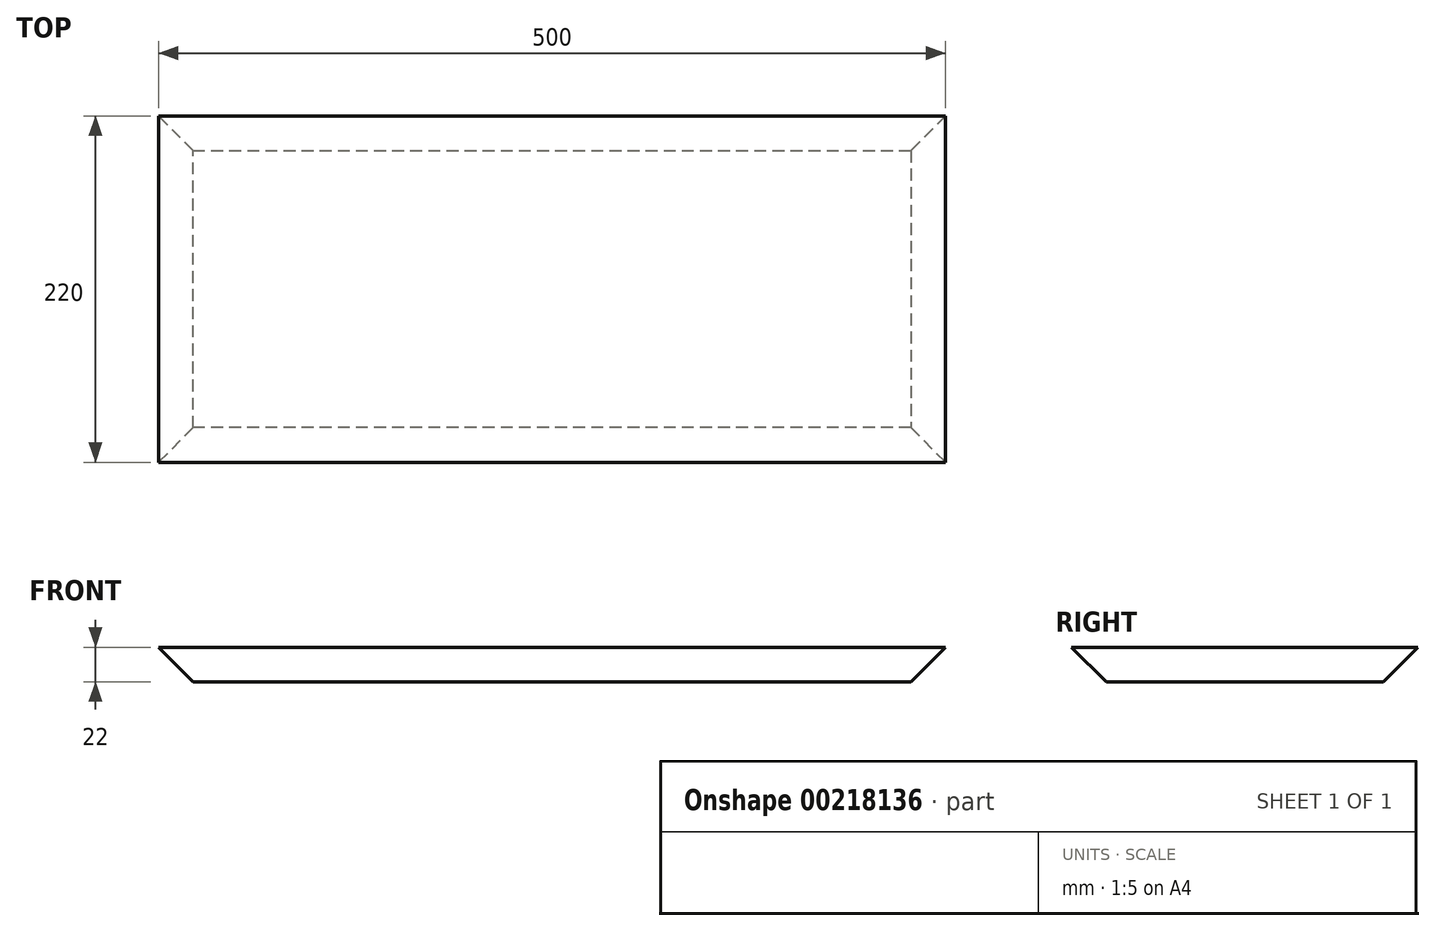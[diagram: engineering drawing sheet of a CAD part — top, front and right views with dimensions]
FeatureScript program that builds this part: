
annotation { "Feature Type Name" : "Feature", "Feature Type Description" : "" }
export const myFeature = defineFeature(function(context is Context, id is Id, definition is map)
    precondition{}
    {
        {
            var Q0;
            Q0=qCreatedBy(makeId("Top.planeOp"),FACE);
            var sketch = newSketch(context, id + "F0", { "sketchPlane" : qUnion([Q0])});
            skLineSegment(sketch, "E0.bottom", {"start": v(250, 110) * mm, "end": v(-250, 110) * mm});
            skLineSegment(sketch, "E0.top", {"start": v(250, -110) * mm, "end": v(-250, -110) * mm});
            skLineSegment(sketch, "E0.left", {"start": v(250, 110) * mm, "end": v(250, -110) * mm});
            skLineSegment(sketch, "E0.right", {"start": v(-250, 110) * mm, "end": v(-250, -110) * mm});
            skPoint(sketch, "E0.middle", {"position": v(0, 0) * mm});
            skSolve(sketch);
        }
        {
            var Q0;
            Q0=makeQuery(id+"F0.imprint","IMPRINT",FACE,{"disambiguationData":[TD([[makeQuery(id+"F0.imprint","IMPRINT",EDGE,{"derivedFrom":sQuery(id+"F0.wireOp",EDGE,"E0.bottom")}),1.0]])]});
            extrude(context, id + "F1", {"entities" : qUnion([Q0]), "depth" : 22 * mm});
        }
        {
            var Q0;
            Q0=makeQuery(id+"F1.opExtrude","CAP_EDGE",EDGE,{"disambiguationData":[OSD([sQuery(id+"F0.wireOp",EDGE,"E0.top")])],"isStart":true});
            var Q1;
            Q1=makeQuery(id+"F1.opExtrude","CAP_EDGE",EDGE,{"disambiguationData":[OSD([sQuery(id+"F0.wireOp",EDGE,"E0.left")])],"isStart":true});
            var Q2;
            Q2=makeQuery(id+"F1.opExtrude","CAP_EDGE",EDGE,{"disambiguationData":[OSD([sQuery(id+"F0.wireOp",EDGE,"E0.bottom")])],"isStart":true});
            var Q3;
            Q3=makeQuery(id+"F1.opExtrude","CAP_EDGE",EDGE,{"disambiguationData":[OSD([sQuery(id+"F0.wireOp",EDGE,"E0.right")])],"isStart":true});
            chamfer(context, id + "F2", {"entities" : qUnion([Q0, Q1, Q2, Q3]), "width" : 22 * mm, "tangentPropagation" : true});
        }
    });
